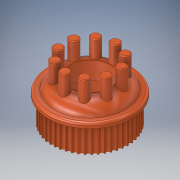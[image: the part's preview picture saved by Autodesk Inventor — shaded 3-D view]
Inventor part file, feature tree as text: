
AUTODESK INVENTOR PART (.ipt)
format: ipt  version: 2019.2 (Build 232265000, 265)  size: 555,520 bytes
history: native  units: mm
features: extrude x7, sketch x6, chamfer x4, pattern_circular x3, fillet x2, plane x1
ambient origin geometry x8: Origin, YZ Plane, XZ Plane, XY Plane, X Axis, Y Axis, Z Axis, Center Point
bodies: Solid1 (feature_tree)
feature tree (23):
  extrude  "Extrusion1"  Depth=25.0mm
  fillet  "Fillet1"  Radius=7.0mm
  extrude  "Extrusion2"  Depth=5.8mm
  chamfer  "Chamfer1"  Distance=18.0mm
  pattern_circular  "Circular Pattern1"  Count=10 Angle=360.0deg
  plane  "Work Plane1"
  sketch  "Sketch3"  dims[d6=15.85mm d7=18.0mm d8=0.0mm]
  extrude  "Extrusion3"  Depth=2.4mm
  fillet  "Fillet2"  Radius=23.873241mm
  chamfer  "Chamfer2"  Distance=4.0mm
  sketch  "Sketch5"  dims[d15=20.0mm d16=2.4mm d17=23.873241mm]
  extrude  "Extrusion4"  Depth=2.5mm
  extrude  "Extrusion5"  Depth=2.5mm TaperAngle=0.0deg
  pattern_circular  "Circular Pattern2"  Angle=45.0deg  [1 undecoded]
  chamfer  "Chamfer3"  Distance=15.0mm
  sketch  "Sketch6"  dims[d18=2.4mm d19=4.0mm d20=0.0mm d21=1.5mm d22=15.0mm d23=0.0mm d24=2.4mm d25=1.0mm d26=45.0deg d27=15.0mm d28=0.0mm d29=500.0mm d30=360.0deg d32=15.0mm d33=3.0mm d34=45.0deg d35=2.0mm d36=2.0mm d37=15.0mm d38=0.0mm d39=15.0mm d40=2.0mm d41=45.0deg d42=2.5mm d43=4.5mm d44=20.0mm d45=0.0mm d46=200.0mm d47=360.0deg]
  extrude  "Extrusion6"  Depth=2.5mm TaperAngle=360.0deg
  chamfer  "Chamfer4"  Distance=15.0mm Angle=45.0deg
  extrude  "Extrusion7"  Depth=2.5mm
  pattern_circular  "Circular Pattern3"  [2 undecoded]
  sketch  "Sketch1"  dims[d0=44.8mm d1=25.0mm d2=7.0mm d3=0.0mm]
  sketch  "Sketch2"  dims[d4=10.0mm d5=5.8mm]
  sketch  "Sketch4"  dims[d9=0.5mm d10=2.0mm d11=45.0deg d12=100.0mm d13=360.0deg]
note: 3 required parameter values undecoded (feature->parameter linkage not recoverable at this tier; creation-order binding heuristic only, values carry confidence <= 0.55)
